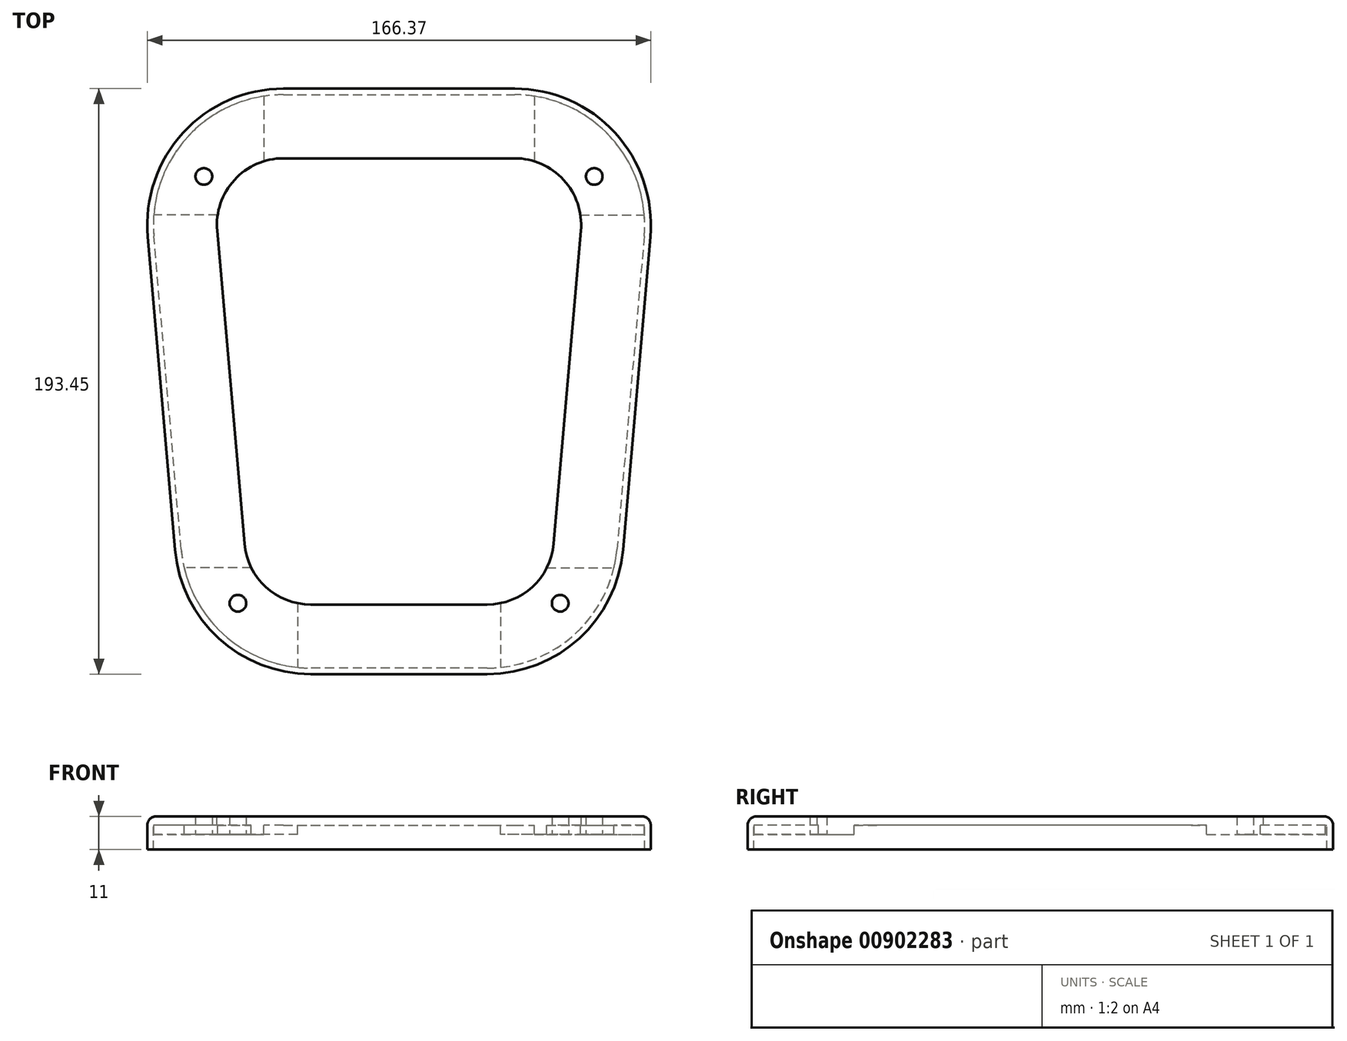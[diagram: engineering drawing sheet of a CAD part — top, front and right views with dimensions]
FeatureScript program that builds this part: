
annotation { "Feature Type Name" : "Feature", "Feature Type Description" : "" }
export const myFeature = defineFeature(function(context is Context, id is Id, definition is map)
    precondition{}
    {
        {
            var Q0;
            Q0=qCreatedBy(makeId("Top.planeOp"),FACE);
            var sketch = newSketch(context, id + "F0", { "sketchPlane" : qUnion([Q0])});
            skLineSegment(sketch, "E0", {"start": v(-36.45, 143.94) * mm, "end": v(39.92, 143.94) * mm});
            skLineSegment(sketch, "E1", {"start": v(1.74, 143.94) * mm, "end": v(1.74, 37.89) * mm, "construction": true});
            skLineSegment(sketch, "E2", {"start": v(-56.37, 122.2) * mm, "end": v(-47.35, 18.75) * mm});
            skLineSegment(sketch, "E3.MirrorCS", {"start": v(59.84, 122.2) * mm, "end": v(50.83, 18.75) * mm});
            skLineSegment(sketch, "E4", {"start": v(-27.43, 0.49) * mm, "end": v(30.9, 0.49) * mm});
            skPoint(sketch, "E5.visualSharp", {"position": v(-45.76, 0.49) * mm});
            skArc(sketch, "E5.filletArc", {"start": v(-47.35, 18.75) * mm, "mid": v(-40.94, 5.74) * mm, "end": v(-27.43, 0.49) * mm});
            skPoint(sketch, "E6.visualSharp", {"position": v(49.24, 0.49) * mm});
            skArc(sketch, "E6.filletArc", {"start": v(30.9, 0.49) * mm, "mid": v(44.42, 5.74) * mm, "end": v(50.83, 18.75) * mm});
            skPoint(sketch, "E7.visualSharp", {"position": v(61.74, 143.94) * mm});
            skArc(sketch, "E7.filletArc", {"start": v(59.84, 122.2) * mm, "mid": v(54.66, 137.46) * mm, "end": v(39.92, 143.94) * mm});
            skPoint(sketch, "E8.visualSharp", {"position": v(-58.26, 143.94) * mm});
            skArc(sketch, "E8.filletArc", {"start": v(-36.45, 143.94) * mm, "mid": v(-51.19, 137.46) * mm, "end": v(-56.37, 122.2) * mm});
            skArc(sketch, "E9.0", {"start": v(-36.45, 148.44) * mm, "mid": v(-54.5, 140.5) * mm, "end": v(-60.85, 121.82) * mm, "construction": true});
            skLineSegment(sketch, "E9.1", {"start": v(-36.45, 148.44) * mm, "end": v(39.92, 148.44) * mm, "construction": true});
            skLineSegment(sketch, "E9.2", {"start": v(-60.85, 121.82) * mm, "end": v(-51.84, 18.36) * mm, "construction": true});
            skArc(sketch, "E9.3", {"start": v(64.33, 121.82) * mm, "mid": v(57.98, 140.5) * mm, "end": v(39.92, 148.44) * mm, "construction": true});
            skArc(sketch, "E9.4", {"start": v(-51.84, 18.36) * mm, "mid": v(-43.99, 2.43) * mm, "end": v(-27.43, -4.01) * mm, "construction": true});
            skLineSegment(sketch, "E9.5", {"start": v(-27.43, -4.01) * mm, "end": v(30.9, -4.01) * mm, "construction": true});
            skArc(sketch, "E9.6", {"start": v(30.9, -4.01) * mm, "mid": v(47.46, 2.43) * mm, "end": v(55.31, 18.36) * mm, "construction": true});
            skLineSegment(sketch, "E9.7", {"start": v(64.33, 121.82) * mm, "end": v(55.31, 18.36) * mm, "construction": true});
            skLineSegment(sketch, "E10.0", {"start": v(-36.45, 139.94) * mm, "end": v(39.92, 139.94) * mm, "construction": true});
            skCircle(sketch, "E11", {"center": v(-62.76, 139.94) * mm, "radius": 2.75 * mm});
            skCircle(sketch, "E12.MirrorC", {"center": v(66.24, 139.94) * mm, "radius": 2.75 * mm});
            skCircle(sketch, "E13", {"center": v(-51.51, -1.1) * mm, "radius": 2.75 * mm});
            skCircle(sketch, "E14.MirrorC", {"center": v(54.99, -1.1) * mm, "radius": 2.75 * mm});
            skLineSegment(sketch, "E15.0", {"start": v(-36.45, 165.94) * mm, "end": v(39.92, 165.94) * mm, "construction": true});
            skArc(sketch, "E15.1", {"start": v(81.76, 120.3) * mm, "mid": v(70.88, 152.32) * mm, "end": v(39.92, 165.94) * mm, "construction": true});
            skArc(sketch, "E15.2", {"start": v(-36.45, 165.94) * mm, "mid": v(-67.4, 152.32) * mm, "end": v(-78.29, 120.3) * mm, "construction": true});
            skLineSegment(sketch, "E15.3", {"start": v(81.76, 120.3) * mm, "end": v(72.74, 16.84) * mm, "construction": true});
            skLineSegment(sketch, "E15.4", {"start": v(-78.29, 120.3) * mm, "end": v(-69.27, 16.84) * mm, "construction": true});
            skArc(sketch, "E15.5", {"start": v(-69.27, 16.84) * mm, "mid": v(-55.81, -10.47) * mm, "end": v(-27.43, -21.51) * mm, "construction": true});
            skLineSegment(sketch, "E15.6", {"start": v(-27.43, -21.51) * mm, "end": v(30.9, -21.51) * mm, "construction": true});
            skArc(sketch, "E15.7", {"start": v(30.9, -21.51) * mm, "mid": v(59.28, -10.47) * mm, "end": v(72.74, 16.84) * mm, "construction": true});
            skLineSegment(sketch, "E16.0", {"start": v(-36.45, 168.94) * mm, "end": v(39.92, 168.94) * mm});
            skArc(sketch, "E16.1", {"start": v(84.75, 120.04) * mm, "mid": v(73.1, 154.35) * mm, "end": v(39.92, 168.94) * mm});
            skArc(sketch, "E16.2", {"start": v(-36.45, 168.94) * mm, "mid": v(-69.62, 154.35) * mm, "end": v(-81.28, 120.04) * mm});
            skLineSegment(sketch, "E16.3", {"start": v(84.75, 120.04) * mm, "end": v(75.73, 16.58) * mm});
            skLineSegment(sketch, "E16.4", {"start": v(-81.28, 120.04) * mm, "end": v(-72.26, 16.58) * mm});
            skArc(sketch, "E16.5", {"start": v(-72.26, 16.58) * mm, "mid": v(-57.84, -12.68) * mm, "end": v(-27.43, -24.51) * mm});
            skLineSegment(sketch, "E16.6", {"start": v(-27.43, -24.51) * mm, "end": v(30.9, -24.51) * mm});
            skArc(sketch, "E16.7", {"start": v(30.9, -24.51) * mm, "mid": v(61.31, -12.68) * mm, "end": v(75.73, 16.58) * mm});
            skSolve(sketch);
        }
        {
            var Q0;
            Q0 = qSketchRegion(id + "F0", true);
            extrude(context, id + "F1", {"entities" : qUnion([Q0]), "depth" : 3 * mm, "offsetDistance" : 25 * mm});
        }
        {
            var Q0;
            Q0=makeQuery(id+"F1.opExtrude","CAP_FACE",FACE,{"disambiguationData":[OSD([sQuery(id+"F0.wireOp",EDGE,"E0"),sQuery(id+"F0.wireOp",EDGE,"E2"),sQuery(id+"F0.wireOp",EDGE,"E3.MirrorCS"),sQuery(id+"F0.wireOp",EDGE,"E4"),sQuery(id+"F0.wireOp",EDGE,"E5.filletArc"),sQuery(id+"F0.wireOp",EDGE,"E6.filletArc"),sQuery(id+"F0.wireOp",EDGE,"E7.filletArc"),sQuery(id+"F0.wireOp",EDGE,"E8.filletArc"),sQuery(id+"F0.wireOp",EDGE,"E11"),sQuery(id+"F0.wireOp",EDGE,"E12.MirrorC"),sQuery(id+"F0.wireOp",EDGE,"E13"),sQuery(id+"F0.wireOp",EDGE,"E14.MirrorC"),sQuery(id+"F0.wireOp",EDGE,"E15.0"),sQuery(id+"F0.wireOp",EDGE,"E15.1"),sQuery(id+"F0.wireOp",EDGE,"E15.2"),sQuery(id+"F0.wireOp",EDGE,"E15.3"),sQuery(id+"F0.wireOp",EDGE,"E15.4"),sQuery(id+"F0.wireOp",EDGE,"E15.5"),sQuery(id+"F0.wireOp",EDGE,"E15.6"),sQuery(id+"F0.wireOp",EDGE,"E15.7")])],"isStart":true});
            var sketch = newSketch(context, id + "F2", { "sketchPlane" : qUnion([Q0])});
            skLineSegment(sketch, "E17", {"start": v(-43.01, -168.46) * mm, "end": v(-43.01, -142.83) * mm});
            skLineSegment(sketch, "E18", {"start": v(-56.18, -127.2) * mm, "end": v(-81.33, -127.2) * mm});
            skLineSegment(sketch, "E19", {"start": v(1.74, -165.94) * mm, "end": v(1.74, -143.94) * mm, "construction": true});
            skLineSegment(sketch, "E20.MirrorCS", {"start": v(46.49, -168.46) * mm, "end": v(46.49, -142.83) * mm});
            skLineSegment(sketch, "E21.MirrorCS", {"start": v(59.65, -127.2) * mm, "end": v(84.8, -127.2) * mm});
            skArc(sketch, "E22.0", {"start": v(59.65, -127.2) * mm, "mid": v(55.22, -136.82) * mm, "end": v(46.49, -142.83) * mm});
            skArc(sketch, "E23.0", {"start": v(-43.01, -142.83) * mm, "mid": v(-51.75, -136.82) * mm, "end": v(-56.18, -127.2) * mm});
            skLineSegment(sketch, "E24", {"start": v(-31.76, -0.96) * mm, "end": v(-31.76, 24.3) * mm});
            skLineSegment(sketch, "E25", {"start": v(-44.84, -10.64) * mm, "end": v(-71.34, -10.64) * mm});
            skLineSegment(sketch, "E26.MirrorCS", {"start": v(35.24, -0.96) * mm, "end": v(35.24, 24.3) * mm});
            skLineSegment(sketch, "E27.MirrorCS", {"start": v(48.31, -10.64) * mm, "end": v(74.81, -10.64) * mm});
            skArc(sketch, "E28.0", {"start": v(30.9, -0.49) * mm, "mid": v(44.42, -5.74) * mm, "end": v(50.83, -18.75) * mm});
            skArc(sketch, "E29.0", {"start": v(-47.35, -18.75) * mm, "mid": v(-40.94, -5.74) * mm, "end": v(-27.43, -0.49) * mm});
            skPoint(sketch, "E30.orphan", {"position": v(39.92, -165.94) * mm});
            skPoint(sketch, "E31.orphan", {"position": v(-56.37, -127.2) * mm});
            skPoint(sketch, "E32.orphan", {"position": v(-56.37, -122.2) * mm});
            skPoint(sketch, "E33.orphan", {"position": v(-78.29, -120.3) * mm});
            skPoint(sketch, "E34.orphan", {"position": v(-36.45, -143.94) * mm});
            skPoint(sketch, "E35.orphan", {"position": v(-36.45, -165.94) * mm});
            skPoint(sketch, "E36.orphan", {"position": v(39.92, -143.94) * mm});
            skPoint(sketch, "E37.orphan", {"position": v(59.84, -127.2) * mm});
            skPoint(sketch, "E38.orphan", {"position": v(59.84, -122.2) * mm});
            skPoint(sketch, "E39.orphan", {"position": v(81.76, -120.3) * mm});
            skCircle(sketch, "E40.0", {"center": v(66.24, -139.94) * mm, "radius": 2.75 * mm});
            skCircle(sketch, "E41.0", {"center": v(-62.76, -139.94) * mm, "radius": 2.75 * mm});
            skCircle(sketch, "E42.0", {"center": v(-51.51, 1.1) * mm, "radius": 2.75 * mm});
            skCircle(sketch, "E43.0", {"center": v(54.99, 1.1) * mm, "radius": 2.75 * mm});
            skArc(sketch, "E44.0", {"start": v(-72.26, -16.58) * mm, "mid": v(-57.84, 12.68) * mm, "end": v(-27.43, 24.51) * mm});
            skArc(sketch, "E45.0", {"start": v(30.9, 24.51) * mm, "mid": v(61.31, 12.68) * mm, "end": v(75.73, -16.58) * mm});
            skArc(sketch, "E46.0", {"start": v(84.75, -120.04) * mm, "mid": v(73.1, -154.35) * mm, "end": v(39.92, -168.94) * mm});
            skArc(sketch, "E47.0", {"start": v(-36.45, -168.94) * mm, "mid": v(-69.62, -154.35) * mm, "end": v(-81.28, -120.04) * mm});
            skPoint(sketch, "E48.orphan", {"position": v(-68.26, -10.64) * mm});
            skPoint(sketch, "E49.orphan", {"position": v(-31.76, 21.29) * mm});
            skPoint(sketch, "E50.orphan", {"position": v(35.24, 21.29) * mm});
            skPoint(sketch, "E51.orphan", {"position": v(71.73, -10.64) * mm});
            skPoint(sketch, "E52.orphan", {"position": v(81.8, -127.2) * mm});
            skPoint(sketch, "E53.orphan", {"position": v(46.49, -165.43) * mm});
            skPoint(sketch, "E54.orphan", {"position": v(-78.32, -127.2) * mm});
            skPoint(sketch, "E55.orphan", {"position": v(-43.01, -165.43) * mm});
            skSolve(sketch);
        }
        {
            var Q0;
            Q0 = qSketchRegion(id + "F2", true);
            extrude(context, id + "F3", {"entities" : qUnion([Q0]), "operationType" : NewBodyOperationType.ADD, "depth" : 3 * mm, "offsetDistance" : 25 * mm});
        }
        {
            var Q0;
            {var subQ0=sQuery(id+"F0.wireOp",EDGE,"E16.5");var subQ1=sQuery(id+"F0.wireOp",EDGE,"E16.4");var subQ2=sQuery(id+"F0.wireOp",EDGE,"E2");var subQ3=sQuery(id+"F0.wireOp",EDGE,"E5.filletArc");var subQ4=sQuery(id+"F0.wireOp",EDGE,"E16.2");var subQ5=sQuery(id+"F0.wireOp",EDGE,"E8.filletArc");Q0=makeQuery(id+"F3.boolean.opBoolean","SPLIT",FACE,{"disambiguationData":[TD([makeQuery(id+"F1.opExtrude","SWEPT_FACE",FACE,{"disambiguationData":[OSD([subQ2])]})])],"derivedFrom":makeQuery(id+"F1.opExtrude","CAP_FACE",FACE,{"disambiguationData":[OSD([sQuery(id+"F0.wireOp",EDGE,"E0"),subQ2,sQuery(id+"F0.wireOp",EDGE,"E3.MirrorCS"),sQuery(id+"F0.wireOp",EDGE,"E4"),subQ3,sQuery(id+"F0.wireOp",EDGE,"E6.filletArc"),sQuery(id+"F0.wireOp",EDGE,"E7.filletArc"),subQ5,sQuery(id+"F0.wireOp",EDGE,"E11"),sQuery(id+"F0.wireOp",EDGE,"E12.MirrorC"),sQuery(id+"F0.wireOp",EDGE,"E13"),sQuery(id+"F0.wireOp",EDGE,"E14.MirrorC"),sQuery(id+"F0.wireOp",EDGE,"E16.0"),sQuery(id+"F0.wireOp",EDGE,"E16.1"),subQ4,sQuery(id+"F0.wireOp",EDGE,"E16.3"),subQ1,subQ0,sQuery(id+"F0.wireOp",EDGE,"E16.6"),sQuery(id+"F0.wireOp",EDGE,"E16.7")])],"isStart":true})});}
            var sketch = newSketch(context, id + "F4", { "sketchPlane" : qUnion([Q0])});
            skArc(sketch, "E56.0", {"start": v(-72.26, -16.58) * mm, "mid": v(-71.9, -13.6) * mm, "end": v(-71.34, -10.64) * mm});
            skLineSegment(sketch, "E57.0", {"start": v(-81.28, -120.04) * mm, "end": v(-72.26, -16.58) * mm});
            skArc(sketch, "E58.0.0", {"start": v(-47.35, -18.75) * mm, "mid": v(-46.53, -14.56) * mm, "end": v(-44.84, -10.64) * mm});
            skLineSegment(sketch, "E58.0.1", {"start": v(-69.29, -10.64) * mm, "end": v(-71.34, -10.64) * mm});
            skArc(sketch, "E58.0.2", {"start": v(-71.34, -10.64) * mm, "mid": v(-71.9, -13.6) * mm, "end": v(-72.26, -16.58) * mm});
            skLineSegment(sketch, "E58.0.3", {"start": v(-72.26, -16.58) * mm, "end": v(-81.28, -120.04) * mm});
            skArc(sketch, "E58.0.4", {"start": v(-81.28, -120.04) * mm, "mid": v(-81.44, -123.61) * mm, "end": v(-81.33, -127.2) * mm});
            skLineSegment(sketch, "E58.0.5", {"start": v(-81.33, -127.2) * mm, "end": v(-79.32, -127.2) * mm});
            skArc(sketch, "E58.0.6", {"start": v(-56.18, -127.2) * mm, "mid": v(-56.43, -124.7) * mm, "end": v(-56.37, -122.2) * mm});
            skLineSegment(sketch, "E58.0.7", {"start": v(-56.37, -122.2) * mm, "end": v(-47.35, -18.75) * mm});
            skArc(sketch, "E59.0.0", {"start": v(39.92, -168.94) * mm, "mid": v(43.21, -168.82) * mm, "end": v(46.49, -168.46) * mm});
            skLineSegment(sketch, "E59.0.1", {"start": v(46.49, -168.46) * mm, "end": v(46.49, -166.44) * mm});
            skArc(sketch, "E59.0.2", {"start": v(46.49, -142.83) * mm, "mid": v(43.25, -143.66) * mm, "end": v(39.92, -143.94) * mm});
            skLineSegment(sketch, "E59.0.3", {"start": v(39.92, -143.94) * mm, "end": v(-36.45, -143.94) * mm});
            skArc(sketch, "E59.0.4", {"start": v(-36.45, -143.94) * mm, "mid": v(-39.78, -143.66) * mm, "end": v(-43.01, -142.83) * mm});
            skLineSegment(sketch, "E59.0.5", {"start": v(-43.01, -166.44) * mm, "end": v(-43.01, -168.46) * mm});
            skArc(sketch, "E59.0.6", {"start": v(-43.01, -168.46) * mm, "mid": v(-39.74, -168.82) * mm, "end": v(-36.45, -168.94) * mm});
            skLineSegment(sketch, "E59.0.7", {"start": v(-36.45, -168.94) * mm, "end": v(39.92, -168.94) * mm});
            skLineSegment(sketch, "E60.0.0", {"start": v(74.81, -10.64) * mm, "end": v(72.76, -10.64) * mm});
            skArc(sketch, "E60.0.1", {"start": v(48.31, -10.64) * mm, "mid": v(50, -14.56) * mm, "end": v(50.83, -18.75) * mm});
            skLineSegment(sketch, "E60.0.2", {"start": v(50.83, -18.75) * mm, "end": v(59.84, -122.2) * mm});
            skArc(sketch, "E60.0.3", {"start": v(59.84, -122.2) * mm, "mid": v(59.9, -124.7) * mm, "end": v(59.65, -127.2) * mm});
            skLineSegment(sketch, "E60.0.4", {"start": v(82.8, -127.2) * mm, "end": v(84.8, -127.2) * mm});
            skArc(sketch, "E60.0.5", {"start": v(84.8, -127.2) * mm, "mid": v(84.92, -123.61) * mm, "end": v(84.75, -120.04) * mm});
            skLineSegment(sketch, "E60.0.6", {"start": v(84.75, -120.04) * mm, "end": v(75.73, -16.58) * mm});
            skArc(sketch, "E60.0.7", {"start": v(75.73, -16.58) * mm, "mid": v(75.37, -13.6) * mm, "end": v(74.81, -10.64) * mm});
            skArc(sketch, "E61.0.0", {"start": v(30.9, -0.49) * mm, "mid": v(33.08, -0.6) * mm, "end": v(35.24, -0.96) * mm});
            skLineSegment(sketch, "E61.0.1", {"start": v(35.24, 22.3) * mm, "end": v(35.24, 24.3) * mm});
            skArc(sketch, "E61.0.2", {"start": v(35.24, 24.3) * mm, "mid": v(33.07, 24.46) * mm, "end": v(30.9, 24.51) * mm});
            skLineSegment(sketch, "E61.0.3", {"start": v(30.9, 24.51) * mm, "end": v(-27.43, 24.51) * mm});
            skArc(sketch, "E61.0.4", {"start": v(-27.43, 24.51) * mm, "mid": v(-29.6, 24.46) * mm, "end": v(-31.76, 24.3) * mm});
            skLineSegment(sketch, "E61.0.5", {"start": v(-31.76, 24.3) * mm, "end": v(-31.76, 22.3) * mm});
            skArc(sketch, "E61.0.6", {"start": v(-31.76, -0.96) * mm, "mid": v(-29.6, -0.6) * mm, "end": v(-27.43, -0.49) * mm});
            skLineSegment(sketch, "E61.0.7", {"start": v(-27.43, -0.49) * mm, "end": v(30.9, -0.49) * mm});
            skArc(sketch, "E62.0", {"start": v(-27.43, 22.51) * mm, "mid": v(-29.6, 22.46) * mm, "end": v(-31.76, 22.3) * mm});
            skLineSegment(sketch, "E62.1", {"start": v(30.9, 22.51) * mm, "end": v(-27.43, 22.51) * mm});
            skArc(sketch, "E62.2", {"start": v(35.24, 22.3) * mm, "mid": v(33.07, 22.46) * mm, "end": v(30.9, 22.51) * mm});
            skArc(sketch, "E63.0", {"start": v(73.74, -16.75) * mm, "mid": v(73.36, -13.68) * mm, "end": v(72.76, -10.64) * mm});
            skLineSegment(sketch, "E63.1", {"start": v(82.76, -120.21) * mm, "end": v(73.74, -16.75) * mm});
            skArc(sketch, "E63.2", {"start": v(82.8, -127.2) * mm, "mid": v(82.92, -123.7) * mm, "end": v(82.76, -120.21) * mm});
            skArc(sketch, "E64.0", {"start": v(39.92, -166.94) * mm, "mid": v(43.21, -166.82) * mm, "end": v(46.49, -166.44) * mm});
            skLineSegment(sketch, "E64.1", {"start": v(-36.45, -166.94) * mm, "end": v(39.92, -166.94) * mm});
            skArc(sketch, "E64.2", {"start": v(-43.01, -166.44) * mm, "mid": v(-39.74, -166.82) * mm, "end": v(-36.45, -166.94) * mm});
            skArc(sketch, "E65.0", {"start": v(-79.28, -120.21) * mm, "mid": v(-79.44, -123.7) * mm, "end": v(-79.32, -127.2) * mm});
            skLineSegment(sketch, "E65.1", {"start": v(-70.27, -16.75) * mm, "end": v(-79.28, -120.21) * mm});
            skArc(sketch, "E65.2", {"start": v(-69.29, -10.64) * mm, "mid": v(-69.89, -13.68) * mm, "end": v(-70.27, -16.75) * mm});
            skSolve(sketch);
        }
        {
            var Q0;
            Q0 = qSketchRegion(id + "F4", true);
            extrude(context, id + "F5", {"entities" : qUnion([Q0]), "operationType" : NewBodyOperationType.ADD, "depth" : 8 * mm, "offsetDistance" : 25 * mm});
        }
        {
            var Q0;
            Q0=makeQuery(id+"F3.opExtrude","CAP_FACE",FACE,{"disambiguationData":[OSD([sQuery(id+"F2.wireOp",EDGE,"E17"),sQuery(id+"F2.wireOp",EDGE,"E18"),sQuery(id+"F2.wireOp",EDGE,"E23.0"),sQuery(id+"F2.wireOp",EDGE,"E41.0"),sQuery(id+"F2.wireOp",EDGE,"E47.0")])],"isStart":false});
            var sketch = newSketch(context, id + "F6", { "sketchPlane" : qUnion([Q0])});
            skArc(sketch, "E66.0.0", {"start": v(-43.01, -142.83) * mm, "mid": v(-51.75, -136.82) * mm, "end": v(-56.18, -127.2) * mm});
            skLineSegment(sketch, "E66.0.2", {"start": v(-79.32, -127.2) * mm, "end": v(-81.33, -127.2) * mm});
            skArc(sketch, "E66.0.3", {"start": v(-81.33, -127.2) * mm, "mid": v(-69.42, -154.56) * mm, "end": v(-43.01, -168.46) * mm});
            skLineSegment(sketch, "E66.0.4", {"start": v(-43.01, -168.46) * mm, "end": v(-43.01, -166.44) * mm});
            skLineSegment(sketch, "E66.0.5", {"start": v(-43.01, -166.44) * mm, "end": v(-43.01, -142.83) * mm});
            skLineSegment(sketch, "E67.0.0", {"start": v(82.8, -127.2) * mm, "end": v(59.65, -127.2) * mm});
            skArc(sketch, "E67.0.1", {"start": v(59.65, -127.2) * mm, "mid": v(55.22, -136.82) * mm, "end": v(46.49, -142.83) * mm});
            skLineSegment(sketch, "E67.0.3", {"start": v(46.49, -166.44) * mm, "end": v(46.49, -168.46) * mm});
            skArc(sketch, "E67.0.4", {"start": v(46.49, -168.46) * mm, "mid": v(72.9, -154.56) * mm, "end": v(84.8, -127.2) * mm});
            skLineSegment(sketch, "E67.0.5", {"start": v(84.8, -127.2) * mm, "end": v(82.8, -127.2) * mm});
            skArc(sketch, "E68.0.0", {"start": v(35.24, -0.96) * mm, "mid": v(42.8, -4.41) * mm, "end": v(48.31, -10.64) * mm});
            skLineSegment(sketch, "E68.0.2", {"start": v(72.76, -10.64) * mm, "end": v(74.81, -10.64) * mm});
            skArc(sketch, "E68.0.3", {"start": v(74.81, -10.64) * mm, "mid": v(60.69, 13.24) * mm, "end": v(35.24, 24.3) * mm});
            skLineSegment(sketch, "E68.0.4", {"start": v(35.24, 24.3) * mm, "end": v(35.24, 22.3) * mm});
            skLineSegment(sketch, "E68.0.5", {"start": v(35.24, 22.3) * mm, "end": v(35.24, -0.96) * mm});
            skLineSegment(sketch, "E69.0.0", {"start": v(-69.29, -10.64) * mm, "end": v(-44.84, -10.64) * mm});
            skArc(sketch, "E69.0.1", {"start": v(-44.84, -10.64) * mm, "mid": v(-39.33, -4.41) * mm, "end": v(-31.76, -0.96) * mm});
            skLineSegment(sketch, "E69.0.3", {"start": v(-31.76, 22.3) * mm, "end": v(-31.76, 24.3) * mm});
            skArc(sketch, "E69.0.4", {"start": v(-31.76, 24.3) * mm, "mid": v(-57.22, 13.24) * mm, "end": v(-71.34, -10.64) * mm});
            skLineSegment(sketch, "E69.0.5", {"start": v(-71.34, -10.64) * mm, "end": v(-69.29, -10.64) * mm});
            skArc(sketch, "E70.0", {"start": v(-31.57, 22.31) * mm, "mid": v(-55.9, 11.75) * mm, "end": v(-69.39, -11.08) * mm});
            skArc(sketch, "E71.0", {"start": v(72.86, -11.08) * mm, "mid": v(59.36, 11.75) * mm, "end": v(35.04, 22.31) * mm});
            skArc(sketch, "E72.0", {"start": v(46.2, -166.48) * mm, "mid": v(71.43, -153.2) * mm, "end": v(82.8, -127.05) * mm});
            skArc(sketch, "E73.0", {"start": v(-79.33, -127.05) * mm, "mid": v(-67.96, -153.2) * mm, "end": v(-42.72, -166.48) * mm});
            skSolve(sketch);
        }
        {
            var Q0;
            Q0 = qSketchRegion(id + "F6", true);
            var Q1;
            Q1=makeQuery(id+"F5.opExtrude","CAP_FACE",FACE,{"disambiguationData":[OSD([sQuery(id+"F4.wireOp",EDGE,"E58.0.1"),sQuery(id+"F4.wireOp",EDGE,"E58.0.2"),sQuery(id+"F4.wireOp",EDGE,"E58.0.3"),sQuery(id+"F4.wireOp",EDGE,"E58.0.4"),sQuery(id+"F4.wireOp",EDGE,"E58.0.5"),sQuery(id+"F4.wireOp",EDGE,"E65.0"),sQuery(id+"F4.wireOp",EDGE,"E65.1"),sQuery(id+"F4.wireOp",EDGE,"E65.2")])],"isStart":false});
            extrude(context, id + "F7", {"entities" : qUnion([Q0]), "operationType" : NewBodyOperationType.ADD, "endBound" : BoundingType.UP_TO_SURFACE, "depth" : 25 * mm, "endBoundEntityFace" : qUnion([Q1]), "offsetDistance" : 25 * mm});
        }
        {
            var Q0;
            Q0=makeQuery(id+"F1.opExtrude","CAP_EDGE",EDGE,{"disambiguationData":[OSD([sQuery(id+"F0.wireOp",EDGE,"E16.0")])],"isStart":false});
            fillet(context, id + "F8", {"entities" : qUnion([Q0]), "radius" : 3 * mm, "tangentPropagation" : true, "allowEdgeOverflow" : false});
        }
        {
            var Q0;
            Q0=makeQuery(id+"F1.opExtrude","CAP_FACE",FACE,{"disambiguationData":[OSD([sQuery(id+"F0.wireOp",EDGE,"E0"),sQuery(id+"F0.wireOp",EDGE,"E2"),sQuery(id+"F0.wireOp",EDGE,"E3.MirrorCS"),sQuery(id+"F0.wireOp",EDGE,"E4"),sQuery(id+"F0.wireOp",EDGE,"E5.filletArc"),sQuery(id+"F0.wireOp",EDGE,"E6.filletArc"),sQuery(id+"F0.wireOp",EDGE,"E7.filletArc"),sQuery(id+"F0.wireOp",EDGE,"E8.filletArc"),sQuery(id+"F0.wireOp",EDGE,"E11"),sQuery(id+"F0.wireOp",EDGE,"E12.MirrorC"),sQuery(id+"F0.wireOp",EDGE,"E13"),sQuery(id+"F0.wireOp",EDGE,"E14.MirrorC"),sQuery(id+"F0.wireOp",EDGE,"E16.0"),sQuery(id+"F0.wireOp",EDGE,"E16.1"),sQuery(id+"F0.wireOp",EDGE,"E16.2"),sQuery(id+"F0.wireOp",EDGE,"E16.3"),sQuery(id+"F0.wireOp",EDGE,"E16.4"),sQuery(id+"F0.wireOp",EDGE,"E16.5"),sQuery(id+"F0.wireOp",EDGE,"E16.6"),sQuery(id+"F0.wireOp",EDGE,"E16.7")])],"isStart":false});
            var sketch = newSketch(context, id + "F9", { "sketchPlane" : qUnion([Q0])});
            skArc(sketch, "E74.0.0", {"start": v(-69.27, 16.84) * mm, "mid": v(-55.81, -10.47) * mm, "end": v(-27.43, -21.51) * mm});
            skLineSegment(sketch, "E74.0.1", {"start": v(-27.43, -21.51) * mm, "end": v(30.9, -21.51) * mm});
            skArc(sketch, "E74.0.2", {"start": v(30.9, -21.51) * mm, "mid": v(59.28, -10.47) * mm, "end": v(72.74, 16.84) * mm});
            skArc(sketch, "E74.0.4", {"start": v(81.76, 120.3) * mm, "mid": v(70.88, 152.32) * mm, "end": v(39.92, 165.94) * mm});
            skLineSegment(sketch, "E74.0.5", {"start": v(39.92, 165.94) * mm, "end": v(-36.45, 165.94) * mm});
            skArc(sketch, "E74.0.6", {"start": v(-36.45, 165.94) * mm, "mid": v(-67.4, 152.32) * mm, "end": v(-78.29, 120.3) * mm});
            skLineSegment(sketch, "E74.0.7", {"start": v(-78.29, 120.3) * mm, "end": v(-69.27, 16.84) * mm});
            skLineSegment(sketch, "E75.0", {"start": v(-36.45, 145.94) * mm, "end": v(39.92, 145.94) * mm});
            skArc(sketch, "E75.1", {"start": v(61.83, 122.03) * mm, "mid": v(56.14, 138.8) * mm, "end": v(39.92, 145.94) * mm});
            skArc(sketch, "E75.2", {"start": v(-36.45, 145.94) * mm, "mid": v(-52.66, 138.8) * mm, "end": v(-58.36, 122.03) * mm});
            skLineSegment(sketch, "E75.3", {"start": v(61.83, 122.03) * mm, "end": v(52.82, 18.58) * mm});
            skLineSegment(sketch, "E75.4", {"start": v(-58.36, 122.03) * mm, "end": v(-49.35, 18.58) * mm});
            skArc(sketch, "E75.5", {"start": v(-49.35, 18.58) * mm, "mid": v(-42.3, 4.27) * mm, "end": v(-27.43, -1.51) * mm});
            skLineSegment(sketch, "E75.6", {"start": v(-27.43, -1.51) * mm, "end": v(30.9, -1.51) * mm});
            skArc(sketch, "E75.7", {"start": v(30.9, -1.51) * mm, "mid": v(45.77, 4.27) * mm, "end": v(52.82, 18.58) * mm});
            skSolve(sketch);
        }
        {
            var Q0;
            Q0 = qSketchRegion(id + "F9", true);
            extrude(context, id + "F10", {"entities" : qUnion([Q0]), "operationType" : NewBodyOperationType.REMOVE, "oppositeDirection" : true, "depth" : 25 * mm, "offsetDistance" : 25 * mm});
        }
    });
